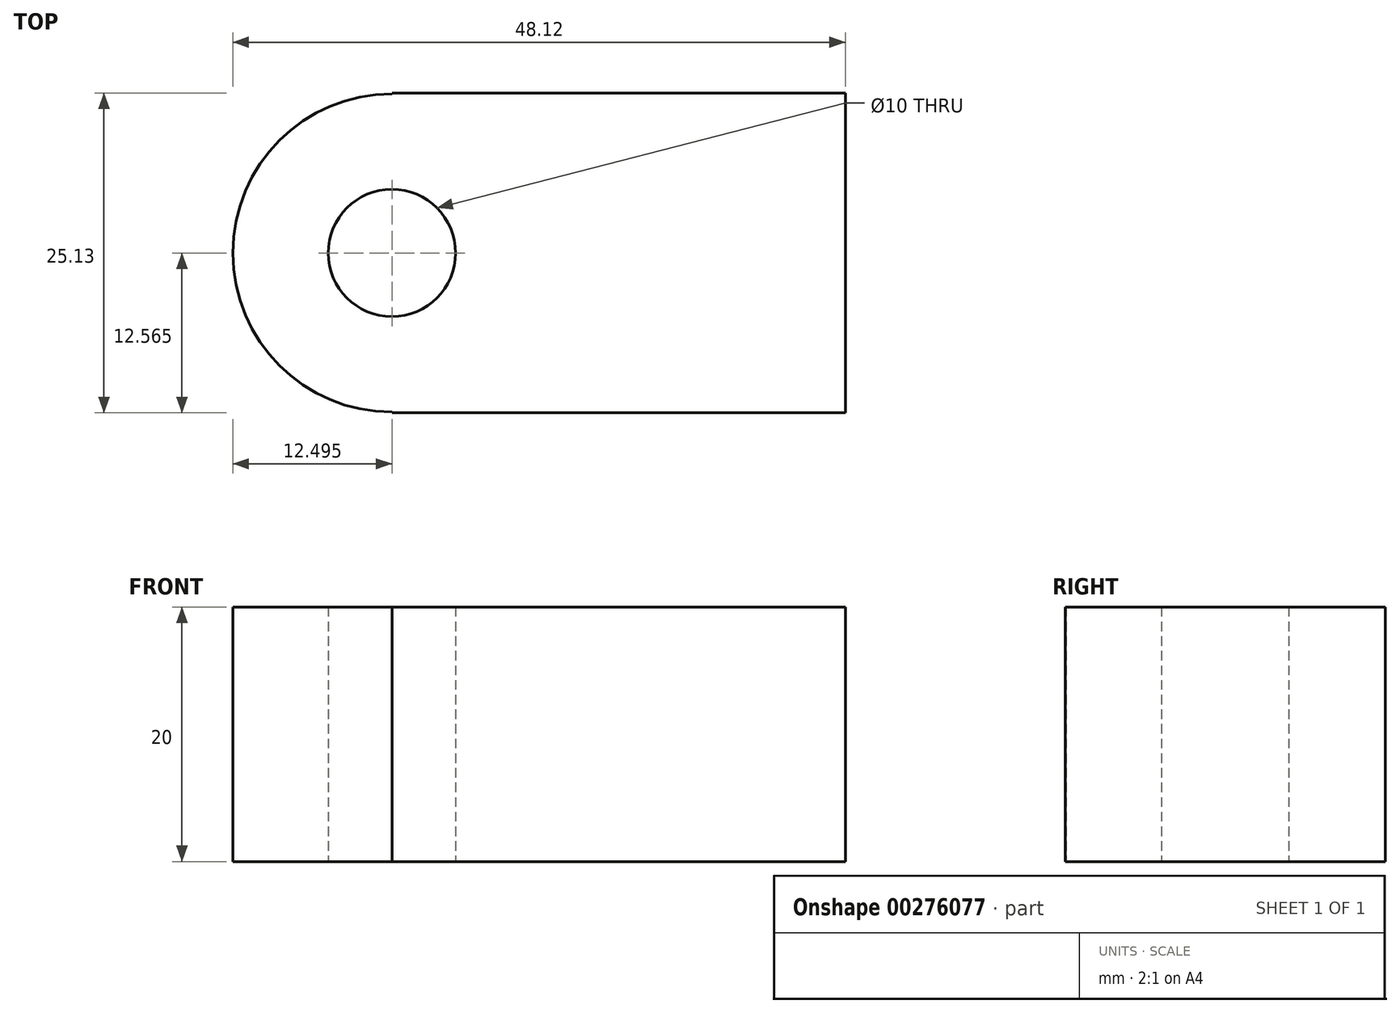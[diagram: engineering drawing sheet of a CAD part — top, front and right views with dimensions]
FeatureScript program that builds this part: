
annotation { "Feature Type Name" : "Feature", "Feature Type Description" : "" }
export const myFeature = defineFeature(function(context is Context, id is Id, definition is map)
    precondition{}
    {
        {
            var Q0;
            Q0=qCreatedBy(makeId("Top.planeOp"),FACE);
            var sketch = newSketch(context, id + "F0", { "sketchPlane" : qUnion([Q0])});
            skLineSegment(sketch, "E0.bottom", {"start": v(-12.4, 11.94) * mm, "end": v(23.22, 11.94) * mm});
            skLineSegment(sketch, "E0.top", {"start": v(-12.4, -13.2) * mm, "end": v(23.22, -13.2) * mm});
            skLineSegment(sketch, "E0.left", {"start": v(-12.4, 11.94) * mm, "end": v(-12.4, -13.2) * mm});
            skLineSegment(sketch, "E0.right", {"start": v(23.22, 11.94) * mm, "end": v(23.22, -13.2) * mm});
            skCircle(sketch, "E1", {"center": v(-12.4, -0.63) * mm, "radius": 12.5 * mm});
            skCircle(sketch, "E2", {"center": v(-12.4, -0.63) * mm, "radius": 5 * mm});
            skSolve(sketch);
        }
        {
            var Q0;
            {var subQ0=sQuery(id+"F0.wireOp",EDGE,"E1");var subQ1=sQuery(id+"F0.wireOp",EDGE,"E0.left");var subQ2=makeQuery(id+"F0.imprint","INTERSECT",VERTEX,{"disambiguationData":[OD(0.0)],"derivedFrom":[subQ1,subQ0]});Q0=makeQuery(id+"F0.imprint","IMPRINT",FACE,{"disambiguationData":[TD([[makeQuery(id+"F0.imprint","IMPRINT",EDGE,{"disambiguationData":[TD([[subQ2,-1.0]])],"derivedFrom":subQ1}),-1.0]])]});}
            var Q1;
            {var subQ0=sQuery(id+"F0.wireOp",EDGE,"E1");var subQ1=sQuery(id+"F0.wireOp",EDGE,"E0.left");var subQ2=makeQuery(id+"F0.imprint","INTERSECT",VERTEX,{"disambiguationData":[OD(0.0)],"derivedFrom":[subQ1,subQ0]});Q1=makeQuery(id+"F0.imprint","IMPRINT",FACE,{"disambiguationData":[TD([[makeQuery(id+"F0.imprint","IMPRINT",EDGE,{"disambiguationData":[TD([[subQ2,-1.0]])],"derivedFrom":subQ1}),1.0]])]});}
            var Q2;
            {var subQ4=sQuery(id+"F0.wireOp",EDGE,"E0.bottom");Q2=makeQuery(id+"F0.imprint","IMPRINT",FACE,{"disambiguationData":[TD([[makeQuery(id+"F0.imprint","IMPRINT",EDGE,{"derivedFrom":subQ4}),-1.0]])]});}
            extrude(context, id + "F1", {"entities" : qUnion([Q0, Q1, Q2]), "depth" : 20 * mm});
        }
    });
